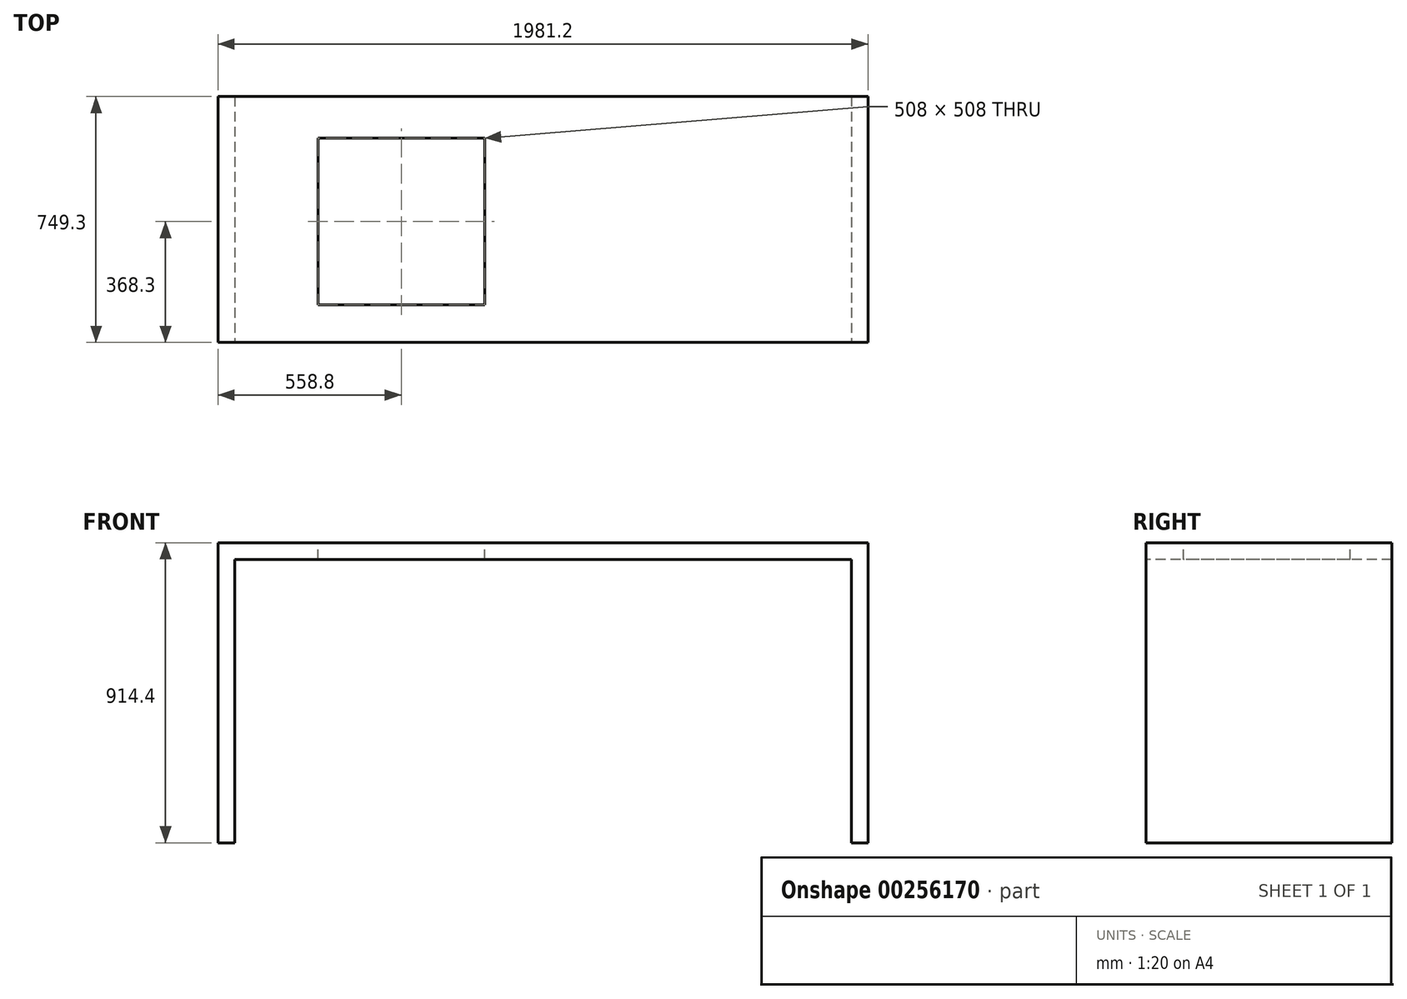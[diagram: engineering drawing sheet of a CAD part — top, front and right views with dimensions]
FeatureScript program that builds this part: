
annotation { "Feature Type Name" : "Feature", "Feature Type Description" : "" }
export const myFeature = defineFeature(function(context is Context, id is Id, definition is map)
    precondition{}
    {
        {
            var Q0;
            Q0=qCreatedBy(makeId("Front.planeOp"),FACE);
            var sketch = newSketch(context, id + "F0", { "sketchPlane" : qUnion([Q0])});
            skLineSegment(sketch, "E0.bottom", {"start": v(0, 0) * mm, "end": v(-1981.2, 0) * mm});
            skLineSegment(sketch, "E0.top", {"start": v(0, 914.4) * mm, "end": v(-1981.2, 914.4) * mm});
            skLineSegment(sketch, "E0.left", {"start": v(0, 0) * mm, "end": v(0, 914.4) * mm});
            skLineSegment(sketch, "E0.right", {"start": v(-1981.2, 0) * mm, "end": v(-1981.2, 914.4) * mm});
            skSolve(sketch);
        }
        {
            var Q0;
            Q0 = qSketchRegion(id + "F0", true);
            extrude(context, id + "F1", {"entities" : qUnion([Q0]), "endBound" : BoundingType.SYMMETRIC, "depth" : 749.3 * mm});
        }
        {
            var Q0;
            Q0=makeQuery(id+"F1.opExtrude","CAP_FACE",FACE,{"disambiguationData":[OSD([sQuery(id+"F0.wireOp",EDGE,"E0.bottom"),sQuery(id+"F0.wireOp",EDGE,"E0.top"),sQuery(id+"F0.wireOp",EDGE,"E0.left"),sQuery(id+"F0.wireOp",EDGE,"E0.right")])],"isStart":false});
            var sketch = newSketch(context, id + "F2", { "sketchPlane" : qUnion([Q0])});
            skLineSegment(sketch, "E1.bottom", {"start": v(-50.8, 0) * mm, "end": v(-1930.4, 0) * mm});
            skLineSegment(sketch, "E1.top", {"start": v(-50.8, 863.6) * mm, "end": v(-1930.4, 863.6) * mm});
            skLineSegment(sketch, "E1.left", {"start": v(-50.8, 0) * mm, "end": v(-50.8, 863.6) * mm});
            skLineSegment(sketch, "E1.right", {"start": v(-1930.4, 0) * mm, "end": v(-1930.4, 863.6) * mm});
            skSolve(sketch);
        }
        {
            var Q0;
            Q0 = qSketchRegion(id + "F2", true);
            extrude(context, id + "F3", {"entities" : qUnion([Q0]), "operationType" : NewBodyOperationType.REMOVE, "endBound" : BoundingType.THROUGH_ALL, "oppositeDirection" : true, "depth" : 25.4 * mm});
        }
        {
            var Q0;
            Q0=makeQuery(id+"F1.opExtrude","SWEPT_FACE",FACE,{"disambiguationData":[OSD([sQuery(id+"F0.wireOp",EDGE,"E0.top")])]});
            var sketch = newSketch(context, id + "F4", { "sketchPlane" : qUnion([Q0])});
            skLineSegment(sketch, "E2.bottom", {"start": v(-1676.4, 247.65) * mm, "end": v(-1168.4, 247.65) * mm});
            skLineSegment(sketch, "E2.top", {"start": v(-1676.4, -260.35) * mm, "end": v(-1168.4, -260.35) * mm});
            skLineSegment(sketch, "E2.left", {"start": v(-1676.4, 247.65) * mm, "end": v(-1676.4, -260.35) * mm});
            skLineSegment(sketch, "E2.right", {"start": v(-1168.4, 247.65) * mm, "end": v(-1168.4, -260.35) * mm});
            skSolve(sketch);
        }
        {
            var Q0;
            Q0 = qSketchRegion(id + "F4", true);
            extrude(context, id + "F5", {"entities" : qUnion([Q0]), "operationType" : NewBodyOperationType.REMOVE, "endBound" : BoundingType.THROUGH_ALL, "oppositeDirection" : true, "depth" : 101.6 * mm});
        }
    });
